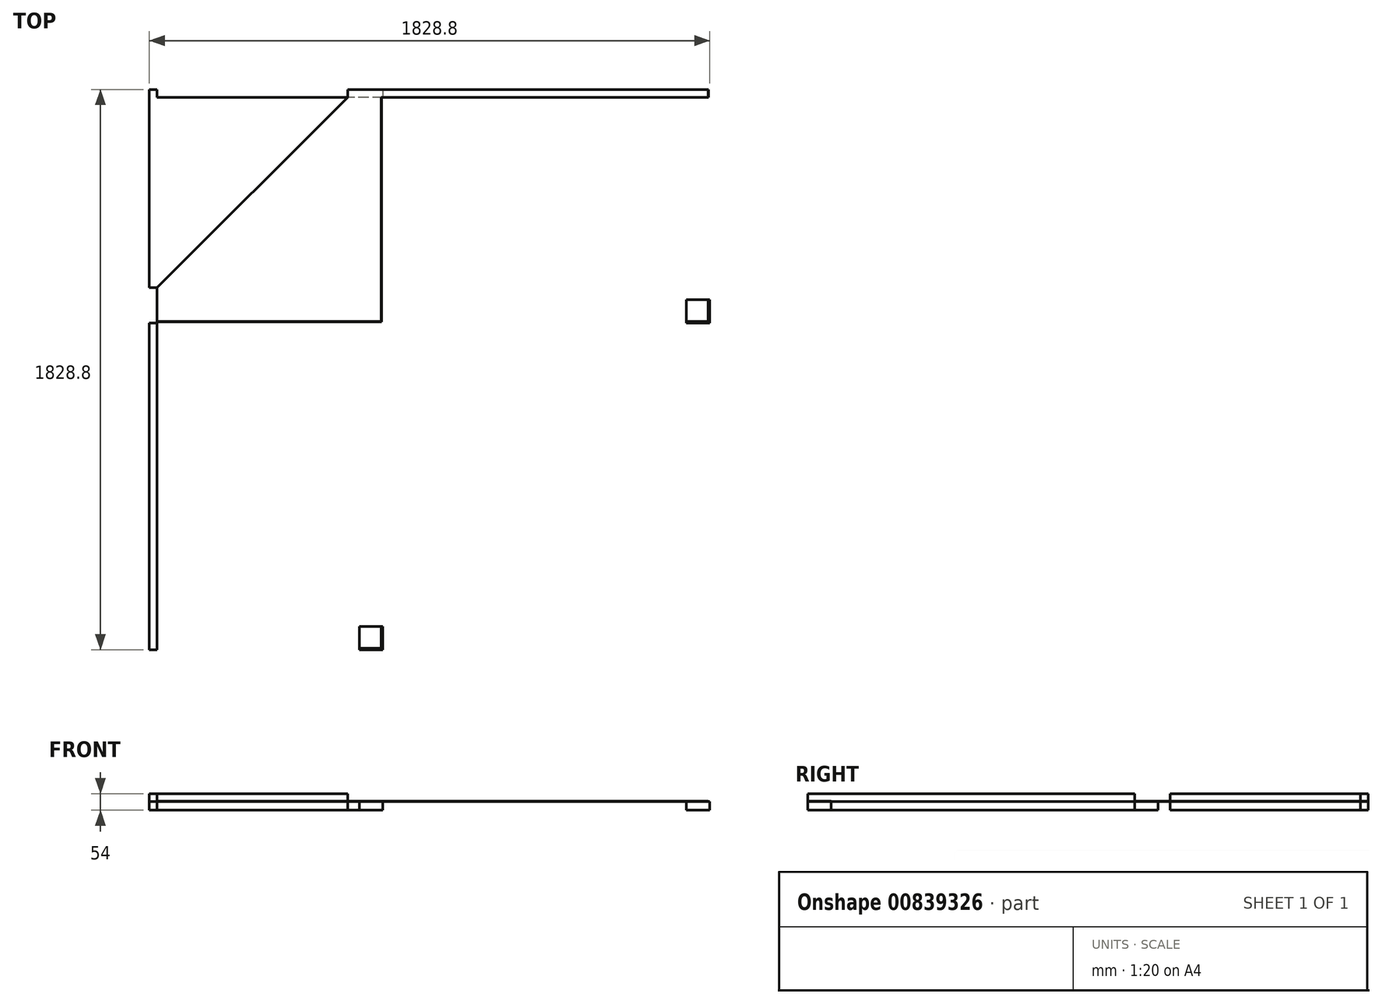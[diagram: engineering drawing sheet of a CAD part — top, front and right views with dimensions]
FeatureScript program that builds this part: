
annotation { "Feature Type Name" : "Feature", "Feature Type Description" : "" }
export const myFeature = defineFeature(function(context is Context, id is Id, definition is map)
    precondition{}
    {
        {
            assignVariable(context, id + "F0", {"name" : "height", "anyValue" : 30});
        }
        {
            assignVariable(context, id + "F1", {"name" : "table_thickness", "anyValue" : 1});
        }
        {
            assignVariable(context, id + "F2", {"name" : "triangle_height", "anyValue" : 24});
        }
        {
            var Q0;
            Q0=qCreatedBy(makeId("Top.planeOp"),FACE);
            var sketch = newSketch(context, id + "F3", { "sketchPlane" : qUnion([Q0])});
            skLineSegment(sketch, "E0.bottom", {"start": v(0, 0) * mm, "end": v(1828.8, 0) * mm});
            skLineSegment(sketch, "E0.top", {"start": v(0, -762) * mm, "end": v(1828.8, -762) * mm});
            skLineSegment(sketch, "E0.left", {"start": v(0, 0) * mm, "end": v(0, -762) * mm});
            skLineSegment(sketch, "E0.right", {"start": v(1828.8, 0) * mm, "end": v(1828.8, -762) * mm});
            skLineSegment(sketch, "E1.bottom", {"start": v(0, 0) * mm, "end": v(762, 0) * mm});
            skLineSegment(sketch, "E1.top", {"start": v(0, -1828.8) * mm, "end": v(762, -1828.8) * mm});
            skLineSegment(sketch, "E1.left", {"start": v(0, 0) * mm, "end": v(0, -1828.8) * mm});
            skLineSegment(sketch, "E1.right", {"start": v(762, 0) * mm, "end": v(762, -1828.8) * mm});
            skLineSegment(sketch, "E2.bottom", {"start": v(762, -1828.8) * mm, "end": v(685.8, -1828.8) * mm});
            skLineSegment(sketch, "E2.top", {"start": v(762, -1752.6) * mm, "end": v(685.8, -1752.6) * mm});
            skLineSegment(sketch, "E2.left", {"start": v(762, -1828.8) * mm, "end": v(762, -1752.6) * mm});
            skLineSegment(sketch, "E2.right", {"start": v(685.8, -1828.8) * mm, "end": v(685.8, -1752.6) * mm});
            skLineSegment(sketch, "E3.bottom", {"start": v(1828.8, -762) * mm, "end": v(1752.6, -762) * mm});
            skLineSegment(sketch, "E3.top", {"start": v(1828.8, -685.8) * mm, "end": v(1752.6, -685.8) * mm});
            skLineSegment(sketch, "E3.left", {"start": v(1828.8, -762) * mm, "end": v(1828.8, -685.8) * mm});
            skLineSegment(sketch, "E3.right", {"start": v(1752.6, -762) * mm, "end": v(1752.6, -685.8) * mm});
            skLineSegment(sketch, "E4.bottom", {"start": v(0, -1828.8) * mm, "end": v(25.4, -1828.8) * mm});
            skLineSegment(sketch, "E4.top", {"start": v(0, 0) * mm, "end": v(25.4, 0) * mm});
            skLineSegment(sketch, "E4.left", {"start": v(0, -1828.8) * mm, "end": v(0, 0) * mm});
            skLineSegment(sketch, "E4.right", {"start": v(25.4, -1828.8) * mm, "end": v(25.4, 0) * mm});
            skLineSegment(sketch, "E5.bottom", {"start": v(1828.8, 0) * mm, "end": v(0, 0) * mm});
            skLineSegment(sketch, "E5.top", {"start": v(1828.8, -25.4) * mm, "end": v(0, -25.4) * mm});
            skLineSegment(sketch, "E5.left", {"start": v(1828.8, 0) * mm, "end": v(1828.8, -25.4) * mm});
            skLineSegment(sketch, "E5.right", {"start": v(0, 0) * mm, "end": v(0, -25.4) * mm});
            skLineSegment(sketch, "E6.bottom", {"start": v(0, 0) * mm, "end": v(646.58, 0) * mm});
            skLineSegment(sketch, "E6.top", {"start": v(0, -646.58) * mm, "end": v(646.58, -646.58) * mm});
            skLineSegment(sketch, "E6.left", {"start": v(0, 0) * mm, "end": v(0, -646.58) * mm});
            skLineSegment(sketch, "E6.right", {"start": v(646.58, 0) * mm, "end": v(646.58, -646.58) * mm});
            skLineSegment(sketch, "E7", {"start": v(0, 0) * mm, "end": v(646.58, -646.58) * mm, "construction": true});
            skLineSegment(sketch, "E8", {"start": v(25.4, -646.58) * mm, "end": v(646.58, -25.4) * mm});
            skSolve(sketch);
        }
        {
            var Q0;
            {var subQ4=sQuery(id+"F3.wireOp",EDGE,"E1.top");Q0=makeQuery(id+"F3.imprint","IMPRINT",FACE,{"disambiguationData":[TD([[makeQuery(id+"F3.imprint","IMPRINT",EDGE,{"derivedFrom":subQ4}),1.0]])]});}
            var Q1;
            {var subQ5=sQuery(id+"F3.wireOp",EDGE,"E4.bottom");Q1=makeQuery(id+"F3.imprint","IMPRINT",FACE,{"disambiguationData":[TD([[makeQuery(id+"F3.imprint","IMPRINT",EDGE,{"derivedFrom":subQ5}),1.0]])]});}
            var Q2;
            {var subQ0=sQuery(id+"F3.wireOp",EDGE,"E4.left");var subQ1=sQuery(id+"F3.wireOp",EDGE,"E0.top");var subQ2=makeQuery(id+"F3.imprint","INTERSECT",VERTEX,{"derivedFrom":[subQ1,subQ0]});Q2=makeQuery(id+"F3.imprint","IMPRINT",FACE,{"disambiguationData":[TD([[makeQuery(id+"F3.imprint","IMPRINT",EDGE,{"disambiguationData":[TD([[subQ2,-1.0]])],"derivedFrom":subQ1}),1.0]])]});}
            var Q3;
            {var subQ1=sQuery(id+"F3.wireOp",EDGE,"E0.top");var subQ6=sQuery(id+"F3.wireOp",EDGE,"E1.right");var subQ11=makeQuery(id+"F3.imprint","INTERSECT",VERTEX,{"derivedFrom":[subQ1,subQ6]});Q3=makeQuery(id+"F3.imprint","IMPRINT",FACE,{"disambiguationData":[TD([[makeQuery(id+"F3.imprint","IMPRINT",EDGE,{"disambiguationData":[TD([[subQ11,1.0]])],"derivedFrom":subQ1}),1.0]])]});}
            var Q4;
            {var subQ6=sQuery(id+"F3.wireOp",EDGE,"E0.right");Q4=makeQuery(id+"F3.imprint","IMPRINT",FACE,{"disambiguationData":[TD([[makeQuery(id+"F3.imprint","IMPRINT",EDGE,{"derivedFrom":subQ6}),-1.0]])]});}
            var Q5;
            Q5=makeQuery(id+"F3.imprint","IMPRINT",FACE,{"disambiguationData":[TD([[makeQuery(id+"F3.imprint","IMPRINT",EDGE,{"derivedFrom":sQuery(id+"F3.wireOp",EDGE,"E3.bottom")}),-1.0]])]});
            var Q6;
            Q6=makeQuery(id+"F3.imprint","IMPRINT",FACE,{"disambiguationData":[TD([[makeQuery(id+"F3.imprint","IMPRINT",EDGE,{"derivedFrom":sQuery(id+"F3.wireOp",EDGE,"E2.bottom")}),-1.0]])]});
            var Q7;
            {var subQ5=sQuery(id+"F3.wireOp",EDGE,"E5.left");Q7=makeQuery(id+"F3.imprint","IMPRINT",FACE,{"disambiguationData":[TD([[makeQuery(id+"F3.imprint","IMPRINT",EDGE,{"derivedFrom":subQ5}),-1.0]])]});}
            var Q8;
            {var subQ0=sQuery(id+"F3.wireOp",EDGE,"E5.bottom");var subQ1=sQuery(id+"F3.wireOp",EDGE,"E1.right");var subQ2=makeQuery(id+"F3.imprint","INTERSECT",VERTEX,{"derivedFrom":[subQ1,subQ0]});Q8=makeQuery(id+"F3.imprint","IMPRINT",FACE,{"disambiguationData":[TD([[makeQuery(id+"F3.imprint","IMPRINT",EDGE,{"disambiguationData":[TD([[subQ2,-1.0]])],"derivedFrom":subQ1}),-1.0]])]});}
            var Q9;
            {var subQ0=sQuery(id+"F3.wireOp",EDGE,"E6.bottom");var subQ1=sQuery(id+"F3.wireOp",EDGE,"E4.right");var subQ2=makeQuery(id+"F3.imprint","INTERSECT",VERTEX,{"derivedFrom":[subQ1,subQ0]});Q9=makeQuery(id+"F3.imprint","IMPRINT",FACE,{"disambiguationData":[TD([[makeQuery(id+"F3.imprint","IMPRINT",EDGE,{"disambiguationData":[TD([[subQ2,1.0]])],"derivedFrom":subQ1}),-1.0]])]});}
            var Q10;
            {var subQ0=sQuery(id+"F3.wireOp",EDGE,"E6.top");var subQ1=sQuery(id+"F3.wireOp",EDGE,"E4.right");var subQ2=makeQuery(id+"F3.imprint","INTERSECT",VERTEX,{"derivedFrom":[subQ1,subQ0]});Q10=makeQuery(id+"F3.imprint","IMPRINT",FACE,{"disambiguationData":[TD([[makeQuery(id+"F3.imprint","IMPRINT",EDGE,{"disambiguationData":[TD([[subQ2,-1.0]])],"derivedFrom":subQ1}),1.0]])]});}
            var Q11;
            {var subQ0=sQuery(id+"F3.wireOp",EDGE,"E6.bottom");var subQ1=sQuery(id+"F3.wireOp",EDGE,"E4.right");var subQ2=makeQuery(id+"F3.imprint","INTERSECT",VERTEX,{"derivedFrom":[subQ1,subQ0]});Q11=makeQuery(id+"F3.imprint","IMPRINT",FACE,{"disambiguationData":[TD([[makeQuery(id+"F3.imprint","IMPRINT",EDGE,{"disambiguationData":[TD([[subQ2,1.0]])],"derivedFrom":subQ1}),1.0]])]});}
            var Q12;
            {var subQ0=sQuery(id+"F3.wireOp",EDGE,"E6.top");var subQ1=sQuery(id+"F3.wireOp",EDGE,"E4.right");var subQ2=makeQuery(id+"F3.imprint","INTERSECT",VERTEX,{"derivedFrom":[subQ1,subQ0]});Q12=makeQuery(id+"F3.imprint","IMPRINT",FACE,{"disambiguationData":[TD([[makeQuery(id+"F3.imprint","IMPRINT",EDGE,{"disambiguationData":[TD([[subQ2,-1.0]])],"derivedFrom":subQ1}),-1.0]])]});}
            var Q13;
            {var subQ3=sQuery(id+"F3.wireOp",EDGE,"E8");Q13=makeQuery(id+"F3.imprint","IMPRINT",FACE,{"disambiguationData":[TD([[makeQuery(id+"F3.imprint","IMPRINT",EDGE,{"derivedFrom":subQ3}),-1.0]])]});}
            extrude(context, id + "F4", {"entities" : qUnion([Q0, Q1, Q2, Q3, Q4, Q5, Q6, Q7, Q8, Q9, Q10, Q11, Q12, Q13]), "depth" : (getVariable(context, 'height')) * mm, "offsetDistance" : 25.4 * mm, "hasSecondDirection" : true, "secondDirectionOppositeDirection" : false, "secondDirectionDepth" : (getVariable(context, 'height') - getVariable(context, 'table_thickness')) * mm});
        }
        {
            var Q0;
            Q0=makeQuery(id+"F3.imprint","IMPRINT",FACE,{"disambiguationData":[TD([[makeQuery(id+"F3.imprint","IMPRINT",EDGE,{"derivedFrom":sQuery(id+"F3.wireOp",EDGE,"E2.bottom")}),-1.0]])]});
            var Q1;
            Q1=makeQuery(id+"F3.imprint","IMPRINT",FACE,{"disambiguationData":[TD([[makeQuery(id+"F3.imprint","IMPRINT",EDGE,{"derivedFrom":sQuery(id+"F3.wireOp",EDGE,"E3.bottom")}),-1.0]])]});
            var Q2;
            {var subQ5=sQuery(id+"F3.wireOp",EDGE,"E4.bottom");Q2=makeQuery(id+"F3.imprint","IMPRINT",FACE,{"disambiguationData":[TD([[makeQuery(id+"F3.imprint","IMPRINT",EDGE,{"derivedFrom":subQ5}),1.0]])]});}
            var Q3;
            {var subQ0=sQuery(id+"F3.wireOp",EDGE,"E4.left");var subQ1=sQuery(id+"F3.wireOp",EDGE,"E0.top");var subQ2=makeQuery(id+"F3.imprint","INTERSECT",VERTEX,{"derivedFrom":[subQ1,subQ0]});Q3=makeQuery(id+"F3.imprint","IMPRINT",FACE,{"disambiguationData":[TD([[makeQuery(id+"F3.imprint","IMPRINT",EDGE,{"disambiguationData":[TD([[subQ2,-1.0]])],"derivedFrom":subQ1}),1.0]])]});}
            var Q4;
            {var subQ5=sQuery(id+"F3.wireOp",EDGE,"E5.left");Q4=makeQuery(id+"F3.imprint","IMPRINT",FACE,{"disambiguationData":[TD([[makeQuery(id+"F3.imprint","IMPRINT",EDGE,{"derivedFrom":subQ5}),-1.0]])]});}
            var Q5;
            {var subQ0=sQuery(id+"F3.wireOp",EDGE,"E5.bottom");var subQ1=sQuery(id+"F3.wireOp",EDGE,"E1.right");var subQ2=makeQuery(id+"F3.imprint","INTERSECT",VERTEX,{"derivedFrom":[subQ1,subQ0]});Q5=makeQuery(id+"F3.imprint","IMPRINT",FACE,{"disambiguationData":[TD([[makeQuery(id+"F3.imprint","IMPRINT",EDGE,{"disambiguationData":[TD([[subQ2,-1.0]])],"derivedFrom":subQ1}),-1.0]])]});}
            var Q6;
            {var subQ0=sQuery(id+"F3.wireOp",EDGE,"E6.bottom");var subQ1=sQuery(id+"F3.wireOp",EDGE,"E4.right");var subQ2=makeQuery(id+"F3.imprint","INTERSECT",VERTEX,{"derivedFrom":[subQ1,subQ0]});Q6=makeQuery(id+"F3.imprint","IMPRINT",FACE,{"disambiguationData":[TD([[makeQuery(id+"F3.imprint","IMPRINT",EDGE,{"disambiguationData":[TD([[subQ2,1.0]])],"derivedFrom":subQ1}),-1.0]])]});}
            var Q7;
            {var subQ0=sQuery(id+"F3.wireOp",EDGE,"E6.top");var subQ1=sQuery(id+"F3.wireOp",EDGE,"E4.right");var subQ2=makeQuery(id+"F3.imprint","INTERSECT",VERTEX,{"derivedFrom":[subQ1,subQ0]});Q7=makeQuery(id+"F3.imprint","IMPRINT",FACE,{"disambiguationData":[TD([[makeQuery(id+"F3.imprint","IMPRINT",EDGE,{"disambiguationData":[TD([[subQ2,-1.0]])],"derivedFrom":subQ1}),1.0]])]});}
            var Q8;
            {var subQ0=sQuery(id+"F3.wireOp",EDGE,"E6.bottom");var subQ1=sQuery(id+"F3.wireOp",EDGE,"E4.right");var subQ2=makeQuery(id+"F3.imprint","INTERSECT",VERTEX,{"derivedFrom":[subQ1,subQ0]});Q8=makeQuery(id+"F3.imprint","IMPRINT",FACE,{"disambiguationData":[TD([[makeQuery(id+"F3.imprint","IMPRINT",EDGE,{"disambiguationData":[TD([[subQ2,1.0]])],"derivedFrom":subQ1}),1.0]])]});}
            extrude(context, id + "F5", {"entities" : qUnion([Q0, Q1, Q2, Q3, Q4, Q5, Q6, Q7, Q8]), "depth" : (getVariable(context, 'height') - getVariable(context, 'table_thickness')) * mm, "offsetDistance" : 25.4 * mm});
        }
        {
            var Q0;
            {var subQ0=sQuery(id+"F3.wireOp",EDGE,"E6.top");var subQ1=sQuery(id+"F3.wireOp",EDGE,"E4.right");var subQ2=makeQuery(id+"F3.imprint","INTERSECT",VERTEX,{"derivedFrom":[subQ1,subQ0]});Q0=makeQuery(id+"F3.imprint","IMPRINT",FACE,{"disambiguationData":[TD([[makeQuery(id+"F3.imprint","IMPRINT",EDGE,{"disambiguationData":[TD([[subQ2,-1.0]])],"derivedFrom":subQ1}),1.0]])]});}
            var Q1;
            {var subQ0=sQuery(id+"F3.wireOp",EDGE,"E6.bottom");var subQ1=sQuery(id+"F3.wireOp",EDGE,"E4.right");var subQ2=makeQuery(id+"F3.imprint","INTERSECT",VERTEX,{"derivedFrom":[subQ1,subQ0]});Q1=makeQuery(id+"F3.imprint","IMPRINT",FACE,{"disambiguationData":[TD([[makeQuery(id+"F3.imprint","IMPRINT",EDGE,{"disambiguationData":[TD([[subQ2,1.0]])],"derivedFrom":subQ1}),1.0]])]});}
            var Q2;
            {var subQ0=sQuery(id+"F3.wireOp",EDGE,"E6.bottom");var subQ1=sQuery(id+"F3.wireOp",EDGE,"E4.right");var subQ2=makeQuery(id+"F3.imprint","INTERSECT",VERTEX,{"derivedFrom":[subQ1,subQ0]});Q2=makeQuery(id+"F3.imprint","IMPRINT",FACE,{"disambiguationData":[TD([[makeQuery(id+"F3.imprint","IMPRINT",EDGE,{"disambiguationData":[TD([[subQ2,1.0]])],"derivedFrom":subQ1}),-1.0]])]});}
            extrude(context, id + "F6", {"entities" : qUnion([Q0, Q1, Q2]), "operationType" : NewBodyOperationType.ADD, "depth" : (getVariable(context, 'height') + getVariable(context, 'triangle_height')) * mm, "offsetDistance" : 25.4 * mm, "hasSecondDirection" : true, "secondDirectionOppositeDirection" : false, "secondDirectionDepth" : (getVariable(context, 'height')) * mm});
        }
        {
            var Q0;
            {var subQ0=sQuery(id+"F3.wireOp",EDGE,"E8");Q0=makeQuery(id+"F3.imprint","IMPRINT",FACE,{"disambiguationData":[TD([[makeQuery(id+"F3.imprint","IMPRINT",EDGE,{"derivedFrom":subQ0}),1.0]])]});}
            extrude(context, id + "F7", {"entities" : qUnion([Q0]), "operationType" : NewBodyOperationType.ADD, "depth" : (getVariable(context, 'height') + getVariable(context, 'triangle_height')) * mm, "offsetDistance" : 25.4 * mm, "hasSecondDirection" : true, "secondDirectionOppositeDirection" : false, "secondDirectionDepth" : (getVariable(context, 'height') + getVariable(context, 'triangle_height') - getVariable(context, 'table_thickness')) * mm});
        }
        {
            var Q0;
            Q0=makeQuery(id+"F4.opExtrude","CAP_EDGE",EDGE,{"disambiguationData":[OSD([sQuery(id+"F3.wireOp",EDGE,"E1.top"),sQuery(id+"F3.wireOp",EDGE,"E2.bottom"),sQuery(id+"F3.wireOp",EDGE,"E4.bottom")])],"isStart":false});
            var Q1;
            Q1=makeQuery(id+"F4.opExtrude","CAP_EDGE",EDGE,{"disambiguationData":[OSD([sQuery(id+"F3.wireOp",EDGE,"E1.right"),sQuery(id+"F3.wireOp",EDGE,"E2.left")])],"isStart":false});
            var Q2;
            Q2=makeQuery(id+"F4.opExtrude","CAP_EDGE",EDGE,{"disambiguationData":[OSD([sQuery(id+"F3.wireOp",EDGE,"E0.top"),sQuery(id+"F3.wireOp",EDGE,"E3.bottom")])],"isStart":false});
            var Q3;
            Q3=makeQuery(id+"F4.opExtrude","CAP_EDGE",EDGE,{"disambiguationData":[OSD([sQuery(id+"F3.wireOp",EDGE,"E0.right"),sQuery(id+"F3.wireOp",EDGE,"E3.left"),sQuery(id+"F3.wireOp",EDGE,"E5.left")])],"isStart":false});
            var Q4;
            Q4=makeQuery(id+"F7.opExtrude","CAP_EDGE",EDGE,{"disambiguationData":[OSD([sQuery(id+"F3.wireOp",EDGE,"E8")])],"isStart":false});
            var Q5;
            Q5=makeQuery(id+"F5.opExtrude","SWEPT_EDGE",EDGE,{"disambiguationData":[OSD([sQuery(id+"F3.wireOp",EDGE,"E2.bottom"),sQuery(id+"F3.wireOp",EDGE,"E2.left")])]});
            var Q6;
            Q6=makeQuery(id+"F5.opExtrude","SWEPT_EDGE",EDGE,{"disambiguationData":[OSD([sQuery(id+"F3.wireOp",EDGE,"E3.bottom"),sQuery(id+"F3.wireOp",EDGE,"E3.left")])]});
            chamfer(context, id + "F8", {"entities" : qUnion([Q0, Q1, Q2, Q3, Q4, Q5, Q6]), "width" : 5.08 * mm, "tangentPropagation" : true});
        }
    });
